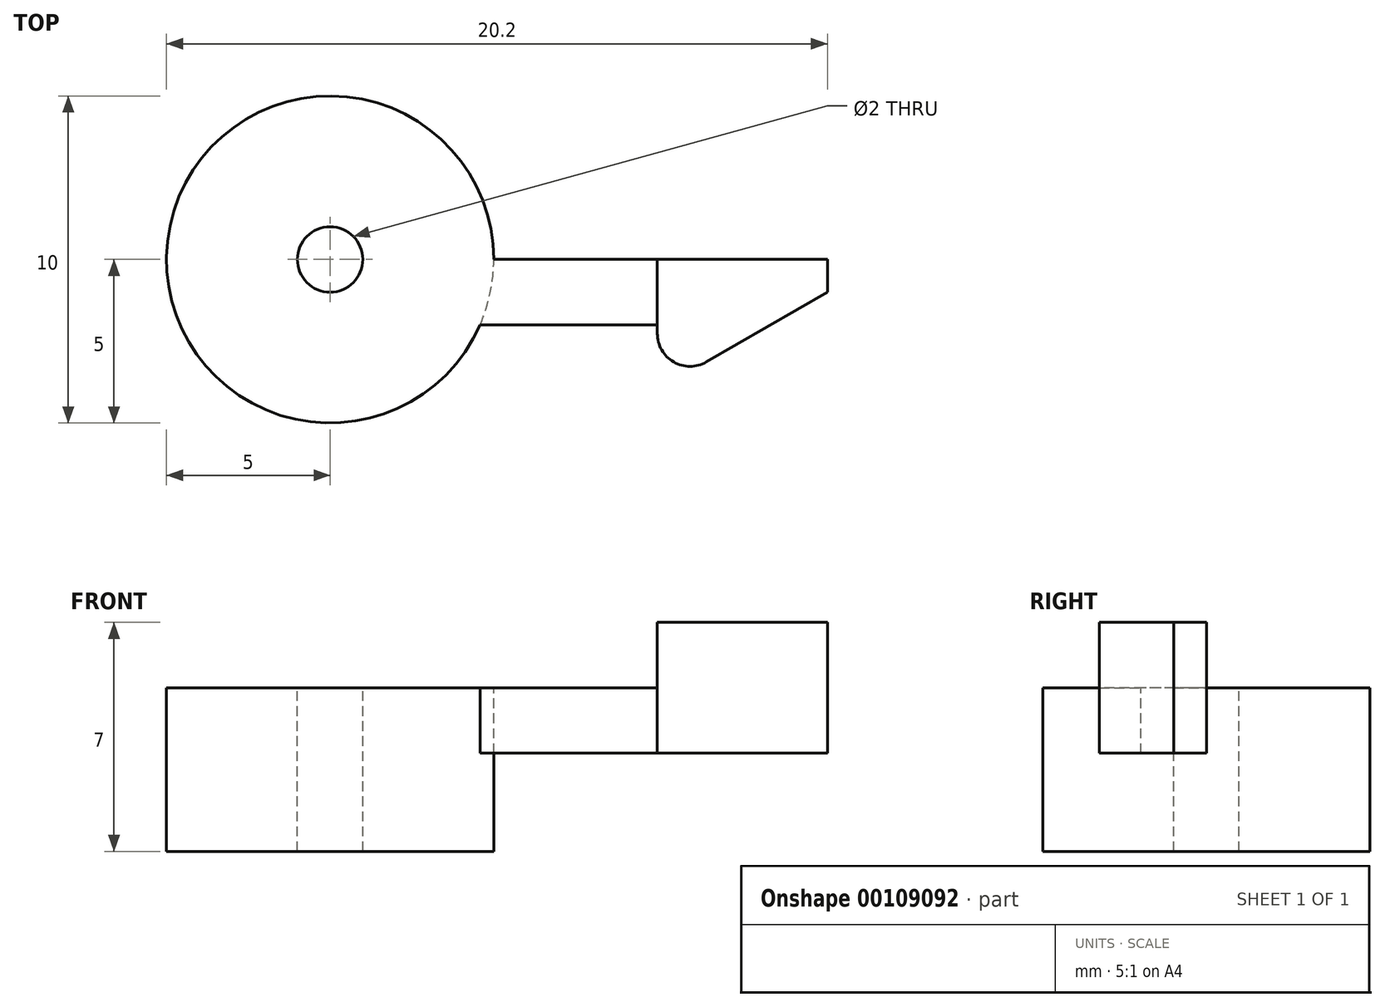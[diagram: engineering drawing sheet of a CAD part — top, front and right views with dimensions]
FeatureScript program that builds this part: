
annotation { "Feature Type Name" : "Feature", "Feature Type Description" : "" }
export const myFeature = defineFeature(function(context is Context, id is Id, definition is map)
    precondition{}
    {
        {
            var Q0;
            Q0=qCreatedBy(makeId("Top.planeOp"),FACE);
            var sketch = newSketch(context, id + "F0", { "sketchPlane" : qUnion([Q0])});
            skCircle(sketch, "E0", {"center": v(0, 0) * mm, "radius": 5 * mm});
            skLineSegment(sketch, "E1", {"start": v(5, 0) * mm, "end": v(10, 0) * mm});
            skLineSegment(sketch, "E2", {"start": v(10, 0) * mm, "end": v(15.2, 0) * mm});
            skLineSegment(sketch, "E3.MirrorCS", {"start": v(10, -2) * mm, "end": v(4.58, -2) * mm});
            skLineSegment(sketch, "E4.MirrorCS", {"start": v(10, -2) * mm, "end": v(10, -4) * mm});
            skLineSegment(sketch, "E5.MirrorCS", {"start": v(10, -4) * mm, "end": v(15.2, -1) * mm});
            skLineSegment(sketch, "E6.MirrorCS", {"start": v(15.2, -1) * mm, "end": v(15.2, 0) * mm});
            skLineSegment(sketch, "E7.MirrorCS", {"start": v(10, 0) * mm, "end": v(10, -2) * mm});
            skSolve(sketch);
        }
        {
            var Q0;
            {var subQ0=sQuery(id+"F0.wireOp",EDGE,"E0");var subQ1=makeQuery(id+"F0.imprint","INTERSECT",VERTEX,{"derivedFrom":[subQ0,sQuery(id+"F0.wireOp",EDGE,"E1")]});Q0=makeQuery(id+"F0.imprint","IMPRINT",FACE,{"disambiguationData":[TD([[makeQuery(id+"F0.imprint","IMPRINT",EDGE,{"disambiguationData":[TD([[subQ1,-1.0]])],"derivedFrom":subQ0}),1.0]])]});}
            extrude(context, id + "F1", {"entities" : qUnion([Q0]), "oppositeDirection" : true, "depth" : 5 * mm});
        }
        {
            var Q0;
            {var subQ0=sQuery(id+"F0.wireOp",EDGE,"E1");Q0=makeQuery(id+"F0.imprint","IMPRINT",FACE,{"disambiguationData":[TD([[makeQuery(id+"F0.imprint","IMPRINT",EDGE,{"derivedFrom":subQ0}),-1.0]])]});}
            extrude(context, id + "F2", {"entities" : qUnion([Q0]), "operationType" : NewBodyOperationType.ADD, "oppositeDirection" : true, "depth" : 2 * mm});
        }
        {
            var Q0;
            Q0=makeQuery(id+"F0.imprint","IMPRINT",FACE,{"disambiguationData":[TD([[makeQuery(id+"F0.imprint","IMPRINT",EDGE,{"derivedFrom":sQuery(id+"F0.wireOp",EDGE,"E2")}),-1.0]])]});
            extrude(context, id + "F3", {"entities" : qUnion([Q0]), "operationType" : NewBodyOperationType.ADD, "endBound" : BoundingType.SYMMETRIC, "depth" : 4 * mm});
        }
        {
            var Q0;
            Q0=makeQuery(id+"F3.opExtrude","SWEPT_EDGE",EDGE,{"disambiguationData":[OSD([sQuery(id+"F0.wireOp",EDGE,"E4.MirrorCS"),sQuery(id+"F0.wireOp",EDGE,"E5.MirrorCS")])]});
            fillet(context, id + "F4", {"entities" : qUnion([Q0]), "radius" : 1 * mm, "tangentPropagation" : true, "allowEdgeOverflow" : false});
        }
        {
            var Q0;
            Q0=sQuery(id+"F0.wireOp",VERTEX,"E0.center");
            var Q1;
            Q1=makeQuery(id+"F1.opExtrude","SWEPT_BODY",BODY,{"disambiguationData":[OSD([sQuery(id+"F0.wireOp",EDGE,"E0")])]});
            hole(context, id + "F5", {"style" : HoleStyle.SIMPLE, "endStyle" : HoleEndStyle.THROUGH, "holeDiameter" : 2 * mm, "locations" : qUnion([Q0]), "scope" : qUnion([Q1]), "isTappedThrough" : true});
        }
    });
